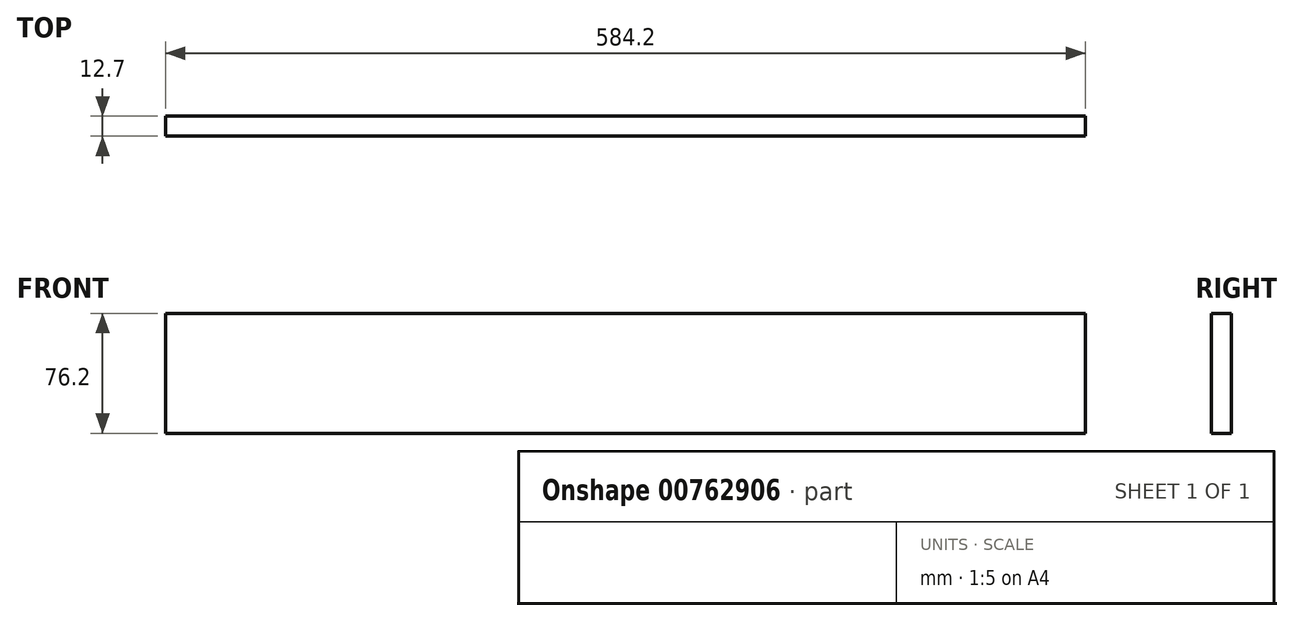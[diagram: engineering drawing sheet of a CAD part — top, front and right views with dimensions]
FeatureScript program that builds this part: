
annotation { "Feature Type Name" : "Feature", "Feature Type Description" : "" }
export const myFeature = defineFeature(function(context is Context, id is Id, definition is map)
    precondition{}
    {
        {
            var Q0;
            Q0=qCreatedBy(makeId("Front.planeOp"),FACE);
            var sketch = newSketch(context, id + "F0", { "sketchPlane" : qUnion([Q0])});
            skLineSegment(sketch, "E0.bottom", {"start": v(-292.1, 38.1) * mm, "end": v(292.1, 38.1) * mm});
            skLineSegment(sketch, "E0.top", {"start": v(-292.1, -38.1) * mm, "end": v(292.1, -38.1) * mm});
            skLineSegment(sketch, "E0.left", {"start": v(-292.1, 38.1) * mm, "end": v(-292.1, -38.1) * mm});
            skLineSegment(sketch, "E0.right", {"start": v(292.1, 38.1) * mm, "end": v(292.1, -38.1) * mm});
            skSolve(sketch);
        }
        {
            var Q0;
            Q0 = qSketchRegion(id + "F0", true);
            extrude(context, id + "F1", {"entities" : qUnion([Q0]), "depth" : 12.7 * mm, "offsetDistance" : 25.4 * mm, "symmetric" : true});
        }
    });
